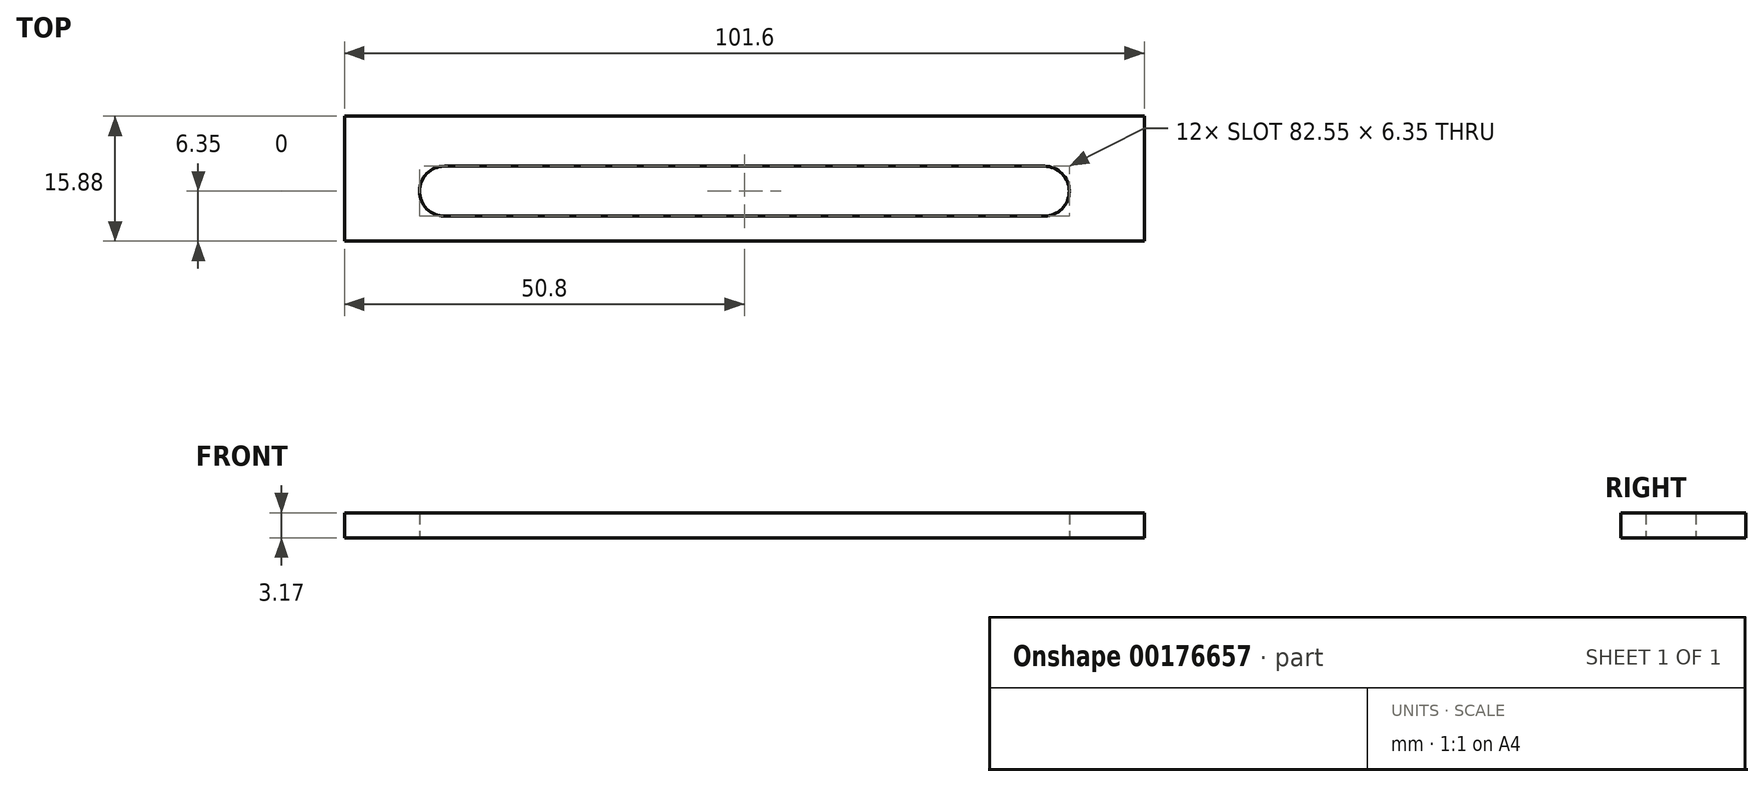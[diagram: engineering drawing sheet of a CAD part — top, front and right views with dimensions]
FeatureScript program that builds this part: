
annotation { "Feature Type Name" : "Feature", "Feature Type Description" : "" }
export const myFeature = defineFeature(function(context is Context, id is Id, definition is map)
    precondition{}
    {
        {
            var Q0;
            Q0=qCreatedBy(makeId("Top.planeOp"),FACE);
            var sketch = newSketch(context, id + "F0", { "sketchPlane" : qUnion([Q0])});
            skLineSegment(sketch, "E0.bottom", {"start": v(0, 0) * mm, "end": v(101.6, 0) * mm});
            skLineSegment(sketch, "E0.top", {"start": v(0, 15.88) * mm, "end": v(101.6, 15.88) * mm});
            skLineSegment(sketch, "E0.left", {"start": v(0, 0) * mm, "end": v(0, 15.88) * mm});
            skLineSegment(sketch, "E0.right", {"start": v(101.6, 0) * mm, "end": v(101.6, 15.88) * mm});
            skLineSegment(sketch, "E1.bottom", {"start": v(12.7, 9.52) * mm, "end": v(88.9, 9.52) * mm});
            skLineSegment(sketch, "E1.top", {"start": v(12.7, 3.18) * mm, "end": v(88.9, 3.18) * mm});
            skArc(sketch, "E2", {"start": v(88.9, 3.18) * mm, "mid": v(92.08, 6.35) * mm, "end": v(88.9, 9.53) * mm});
            skArc(sketch, "E3", {"start": v(12.7, 9.53) * mm, "mid": v(9.53, 6.35) * mm, "end": v(12.7, 3.17) * mm});
            skSolve(sketch);
        }
        {
            var Q0;
            Q0 = qSketchRegion(id + "F0", true);
            extrude(context, id + "F1", {"entities" : qUnion([Q0]), "depth" : 3.17 * mm});
        }
    });
